# Revit family: SV
name_source: partatom
category: Mechanical Equipment
units: mm (PartAtom-declared; Revit-internal decimal feet)

## family parameters
Always vertical = Yes
Cut with Voids When Loaded = No
Part Type = Normal
Room Calculation Point = No
Round Connector Dimension = Use Diameter
Shared = No
Work Plane-Based = No

## types (4) — shared parameters
Case Fans (FLA) = Fans 208V
Case Fans (FLA)-2 = Fans 380V
Case Fans (FLA)-3 = Fans 460V
Case Fans (FLA)-4 = Fans 575V
Copper Pipes = Copper
Description = 4-fan Evaporator
Elect. Defrost Amps-2 = Elect. Def. Htrs. 380V
Elect. Defrost Amps-3 = Elect. Def. Htrs. 460V
Elect. Defrost Amps-4 = Elect. Def. Htrs. 575V
Manufacturer = Krack Corporation
Revit Family Dates = 09/16/2022SV
Type Comments = SV Series 2-Fan Evaporator
URL = www.krack.com
Voltage - 2 = 380 V
Voltage - 3 = 460 V
Voltage - 4 = 575 V
Voltage - Electrical Defrost - 2 = 380 V
Voltage - Electrical Defrost - 3 = 460 V
Voltage - Electrical Defrost - 4 = 575 V
WIDTH = 38.5 "

## per-type parameters (varying)
| type | 1-FAN | 2-FAN | 3-FAN | 4-FAN | FAN HEIGHT | HEIGHT | LENGTH | Phase - 2 | Phase - Elect. Def. - 2 |
| SV4 | No | No | No | Yes | 7.5 " | 52.5 " | 172 " | 3 | 1 |
| SV3 | No | No | Yes | No | 7.5 " | 51 " | 133 " | 1 | 0 |
| SV2 | No | Yes | No | No | 3 " | 40.5 " | 133 " | 1 | 0 |
| SV1 | Yes | No | No | No | 3 " | 40.5 " | 75 " | 1 | 0 |

note: column(s) folded — value = type name in every type: Model

## geometry (parser evidence)
native form markers: Sweep x21
no freeform markers — native parametric forms only
